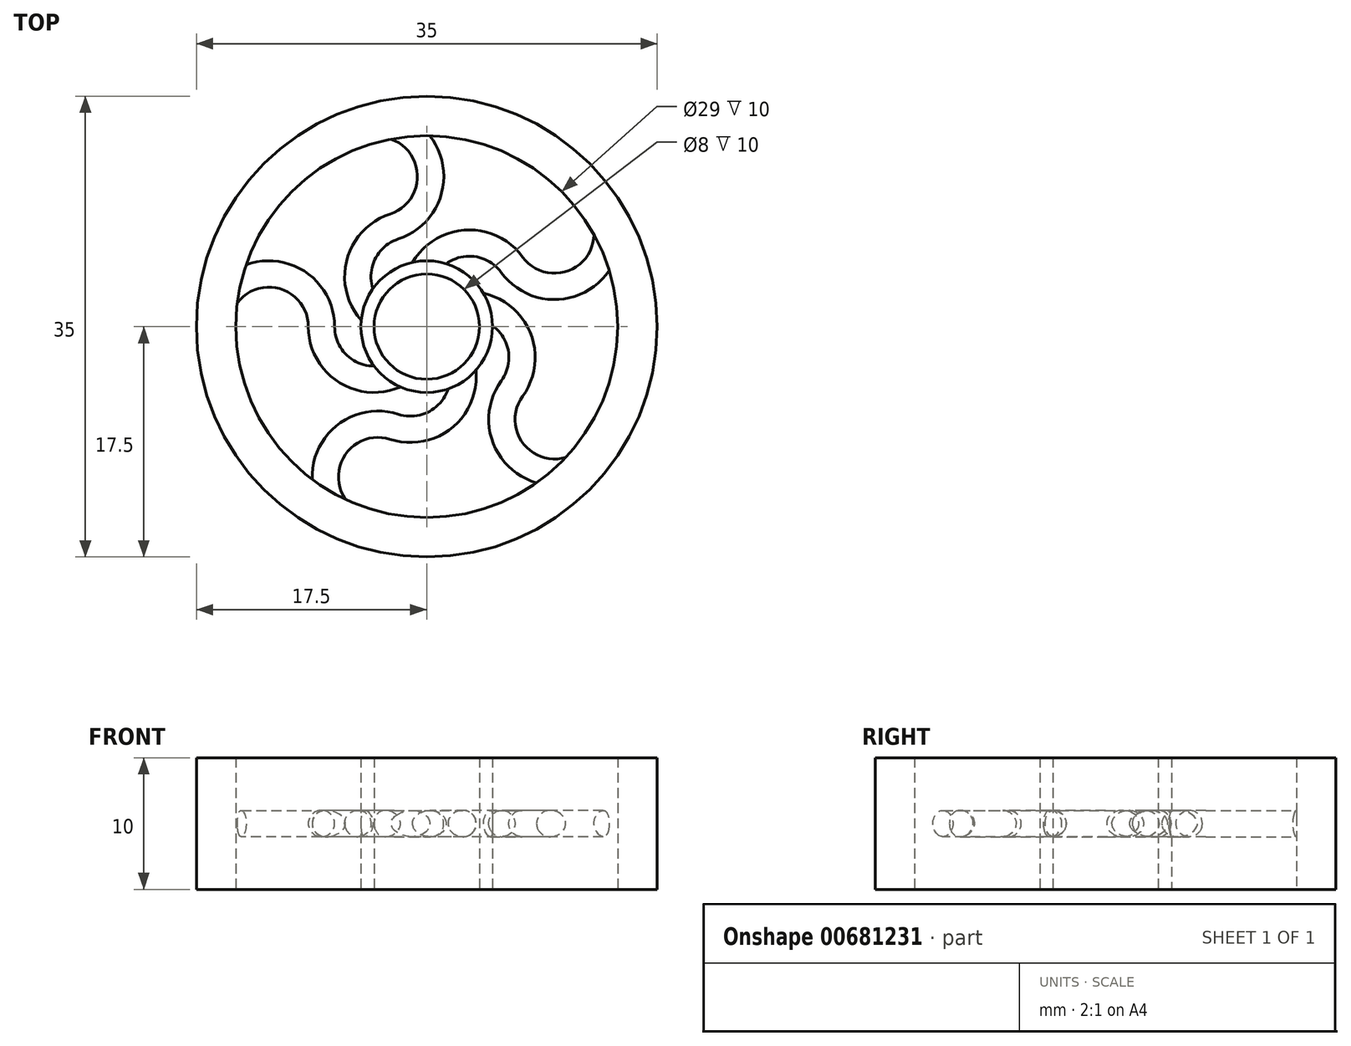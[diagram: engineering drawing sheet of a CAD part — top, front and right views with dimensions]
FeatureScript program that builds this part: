
annotation { "Feature Type Name" : "Feature", "Feature Type Description" : "" }
export const myFeature = defineFeature(function(context is Context, id is Id, definition is map)
    precondition{}
    {
        {
            var Q0;
            Q0=qCreatedBy(makeId("Top.planeOp"),FACE);
            var sketch = newSketch(context, id + "F0", { "sketchPlane" : qUnion([Q0])});
            skArc(sketch, "E0", {"start": v(-8, 0) * mm, "mid": v(-4, -4) * mm, "end": v(0, 0) * mm});
            skArc(sketch, "E1", {"start": v(-8, 0) * mm, "mid": v(-12, 4) * mm, "end": v(-16, 0) * mm});
            skSolve(sketch);
        }
        {
            var Q0;
            Q0=qCreatedBy(makeId("Front.planeOp"),FACE);
            var sketch = newSketch(context, id + "F1", { "sketchPlane" : qUnion([Q0])});
            skCircle(sketch, "E2", {"center": v(0, 0) * mm, "radius": 1 * mm});
            skSolve(sketch);
        }
        {
            var Q0;
            Q0=makeQuery(id+"F1.imprint","IMPRINT",FACE,{"disambiguationData":[TD([[makeQuery(id+"F1.imprint","IMPRINT",EDGE,{"derivedFrom":sQuery(id+"F1.wireOp",EDGE,"E2")}),1.0]])]});
            var Q1;
            Q1=sQuery(id+"F0.wireOp",EDGE,"E0");
            var Q2;
            Q2=sQuery(id+"F0.wireOp",EDGE,"E1");
            sweep(context, id + "F2", {"profiles" : qUnion([Q0]), "path" : qUnion([Q1, Q2])});
        }
        {
            var Q0;
            Q0=qCreatedBy(makeId("Top.planeOp"),FACE);
            var sketch = newSketch(context, id + "F3", { "sketchPlane" : qUnion([Q0])});
            skCircle(sketch, "E3", {"center": v(0, 0) * mm, "radius": 5 * mm});
            skSolve(sketch);
        }
        {
            var Q0;
            Q0=makeQuery(id+"F2.opSweep","SWEPT_BODY",BODY,{"disambiguationData":[OSD([sQuery(id+"F0.wireOp",EDGE,"E1"),sQuery(id+"F1.wireOp",EDGE,"E2")])]});
            var Q1;
            Q1=sQuery(id+"F3.wireOp",EDGE,"E3");
            circularPattern(context, id + "F4", {"entities" : qUnion([Q0]), "axis" : qUnion([Q1]), "angle" : 360 * degree, "instanceCount" : 5, "equalSpace" : true});
        }
        {
            var Q0;
            Q0=qCreatedBy(makeId("Top.planeOp"),FACE);
            var sketch = newSketch(context, id + "F5", { "sketchPlane" : qUnion([Q0])});
            skCircle(sketch, "E4", {"center": v(0, 0) * mm, "radius": 14.5 * mm});
            skCircle(sketch, "E5", {"center": v(0, 0) * mm, "radius": 17.5 * mm});
            skSolve(sketch);
        }
        {
            var Q0;
            Q0 = qSketchRegion(id + "F5", true);
            extrude(context, id + "F6", {"entities" : qUnion([Q0]), "operationType" : NewBodyOperationType.ADD, "depth" : 5 * mm, "offsetDistance" : 25 * mm, "hasSecondDirection" : true, "secondDirectionOppositeDirection" : true, "secondDirectionDepth" : 5 * mm});
        }
        {
            var Q0;
            Q0=qCreatedBy(makeId("Top.planeOp"),FACE);
            var sketch = newSketch(context, id + "F7", { "sketchPlane" : qUnion([Q0])});
            skCircle(sketch, "E6", {"center": v(0, 0) * mm, "radius": 4 * mm});
            skCircle(sketch, "E7", {"center": v(0, 0) * mm, "radius": 5 * mm});
            skSolve(sketch);
        }
        {
            var Q0;
            Q0 = qSketchRegion(id + "F7", true);
            extrude(context, id + "F8", {"entities" : qUnion([Q0]), "operationType" : NewBodyOperationType.ADD, "depth" : 5 * mm, "offsetDistance" : 25 * mm, "hasSecondDirection" : true, "secondDirectionOppositeDirection" : true, "secondDirectionDepth" : 5 * mm});
        }
        {
            var Q0;
            Q0=qCreatedBy(makeId("Top.planeOp"),FACE);
            var sketch = newSketch(context, id + "F9", { "sketchPlane" : qUnion([Q0])});
            skCircle(sketch, "E8", {"center": v(0, 0) * mm, "radius": 4 * mm});
            skSolve(sketch);
        }
        {
            var Q0;
            Q0 = qSketchRegion(id + "F9", true);
            extrude(context, id + "F10", {"entities" : qUnion([Q0]), "operationType" : NewBodyOperationType.REMOVE, "oppositeDirection" : true, "depth" : 25 * mm, "offsetDistance" : 25 * mm, "hasSecondDirection" : true, "secondDirectionOppositeDirection" : false, "secondDirectionDepth" : 25 * mm});
        }
    });
